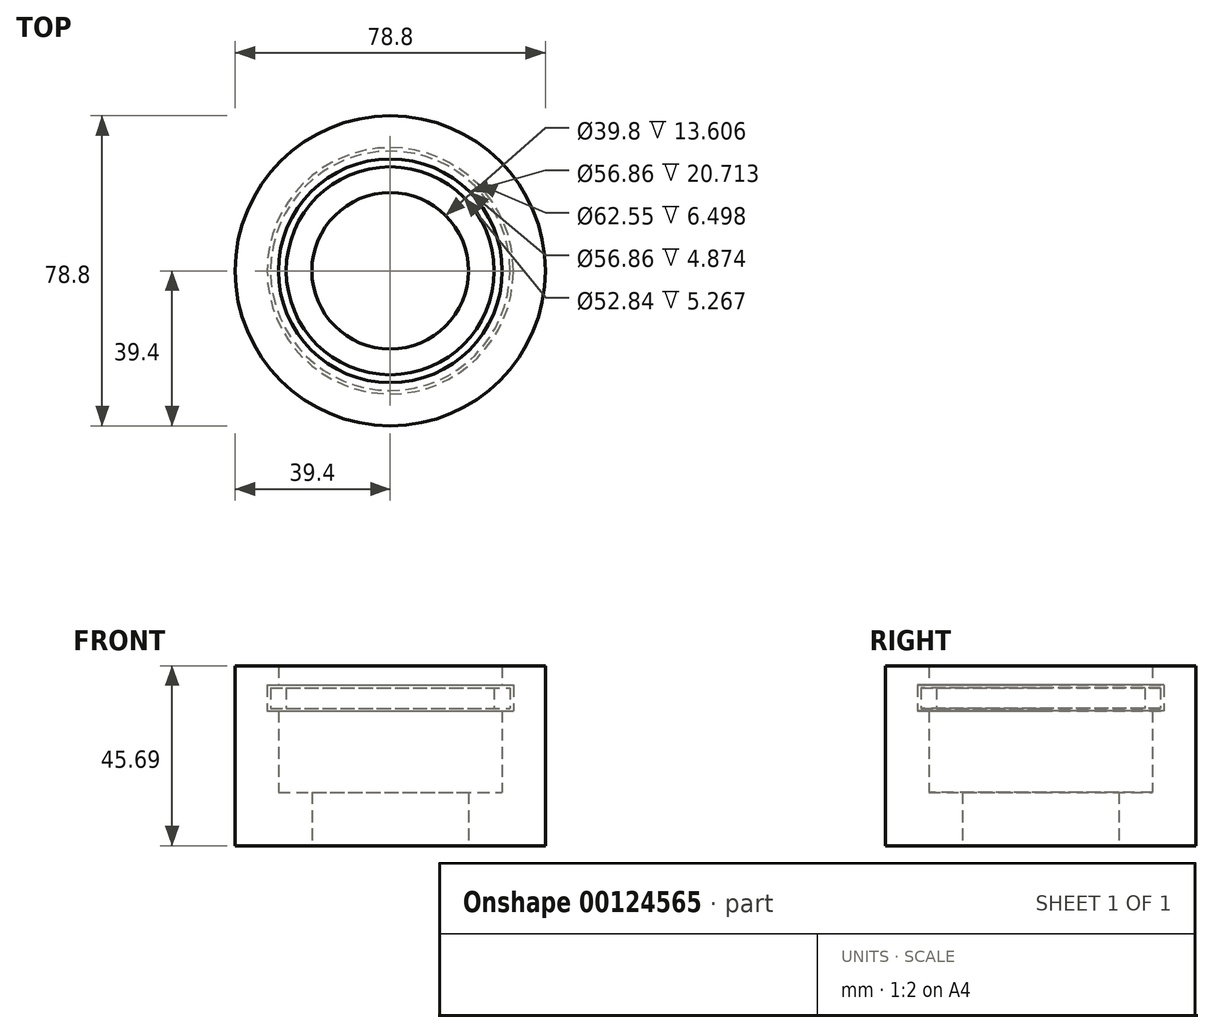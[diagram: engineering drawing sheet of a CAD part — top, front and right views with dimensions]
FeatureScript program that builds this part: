
annotation { "Feature Type Name" : "Feature", "Feature Type Description" : "" }
export const myFeature = defineFeature(function(context is Context, id is Id, definition is map)
    precondition{}
    {
        {
            var Q0;
            Q0=qCreatedBy(makeId("Front.planeOp"),FACE);
            var sketch = newSketch(context, id + "F0", { "sketchPlane" : qUnion([Q0])});
            skLineSegment(sketch, "E0.bottom", {"start": v(-28.43, 0) * mm, "end": v(-39.4, 0) * mm});
            skLineSegment(sketch, "E0.top", {"start": v(-28.43, 45.7) * mm, "end": v(-39.4, 45.7) * mm});
            skLineSegment(sketch, "E0.left", {"start": v(-28.43, 13.6) * mm, "end": v(-28.43, 34.32) * mm});
            skLineSegment(sketch, "E0.right", {"start": v(-39.4, 0) * mm, "end": v(-39.4, 45.7) * mm});
            skLineSegment(sketch, "E1.bottom", {"start": v(-28.43, 13.6) * mm, "end": v(-19.9, 13.6) * mm});
            skLineSegment(sketch, "E1.top", {"start": v(-28.43, 0) * mm, "end": v(-19.9, 0) * mm});
            skLineSegment(sketch, "E1.right", {"start": v(-19.9, 13.6) * mm, "end": v(-19.9, 0) * mm});
            skLineSegment(sketch, "E2.bottom", {"start": v(-28.43, 40.82) * mm, "end": v(-31.27, 40.82) * mm});
            skLineSegment(sketch, "E2.top", {"start": v(-28.43, 34.32) * mm, "end": v(-31.27, 34.32) * mm});
            skLineSegment(sketch, "E2.right", {"start": v(-31.27, 40.82) * mm, "end": v(-31.27, 34.32) * mm});
            skLineSegment(sketch, "E3.trimOffspring", {"start": v(-28.43, 40.82) * mm, "end": v(-28.43, 45.7) * mm});
            skLineSegment(sketch, "E4", {"start": v(0, 0) * mm, "end": v(0, 60.08) * mm, "construction": true});
            skLineSegment(sketch, "E5.bottom", {"start": v(-30.4, 34.87) * mm, "end": v(-26.42, 34.87) * mm});
            skLineSegment(sketch, "E5.top", {"start": v(-30.4, 40.13) * mm, "end": v(-26.42, 40.13) * mm});
            skLineSegment(sketch, "E5.left", {"start": v(-30.4, 34.87) * mm, "end": v(-30.4, 40.13) * mm});
            skLineSegment(sketch, "E5.right", {"start": v(-26.42, 34.87) * mm, "end": v(-26.42, 40.13) * mm});
            skSolve(sketch);
        }
        {
            var Q0;
            Q0=makeQuery(id+"F0.imprint","IMPRINT",FACE,{"disambiguationData":[TD([[makeQuery(id+"F0.imprint","IMPRINT",EDGE,{"derivedFrom":sQuery(id+"F0.wireOp",EDGE,"E0.bottom")}),-1.0]])]});
            var Q1;
            Q1=makeQuery(id+"F0.imprint","IMPRINT",FACE,{"disambiguationData":[TD([[makeQuery(id+"F0.imprint","IMPRINT",EDGE,{"derivedFrom":sQuery(id+"F0.wireOp",EDGE,"E5.bottom")}),1.0]])]});
            var Q2;
            Q2=sQuery(id+"F0.wireOp",EDGE,"E4");
            revolve(context, id + "F1", {"entities" : qUnion([Q0, Q1]), "axis" : qUnion([Q2]), "revolveType" : RevolveType.FULL});
        }
    });
